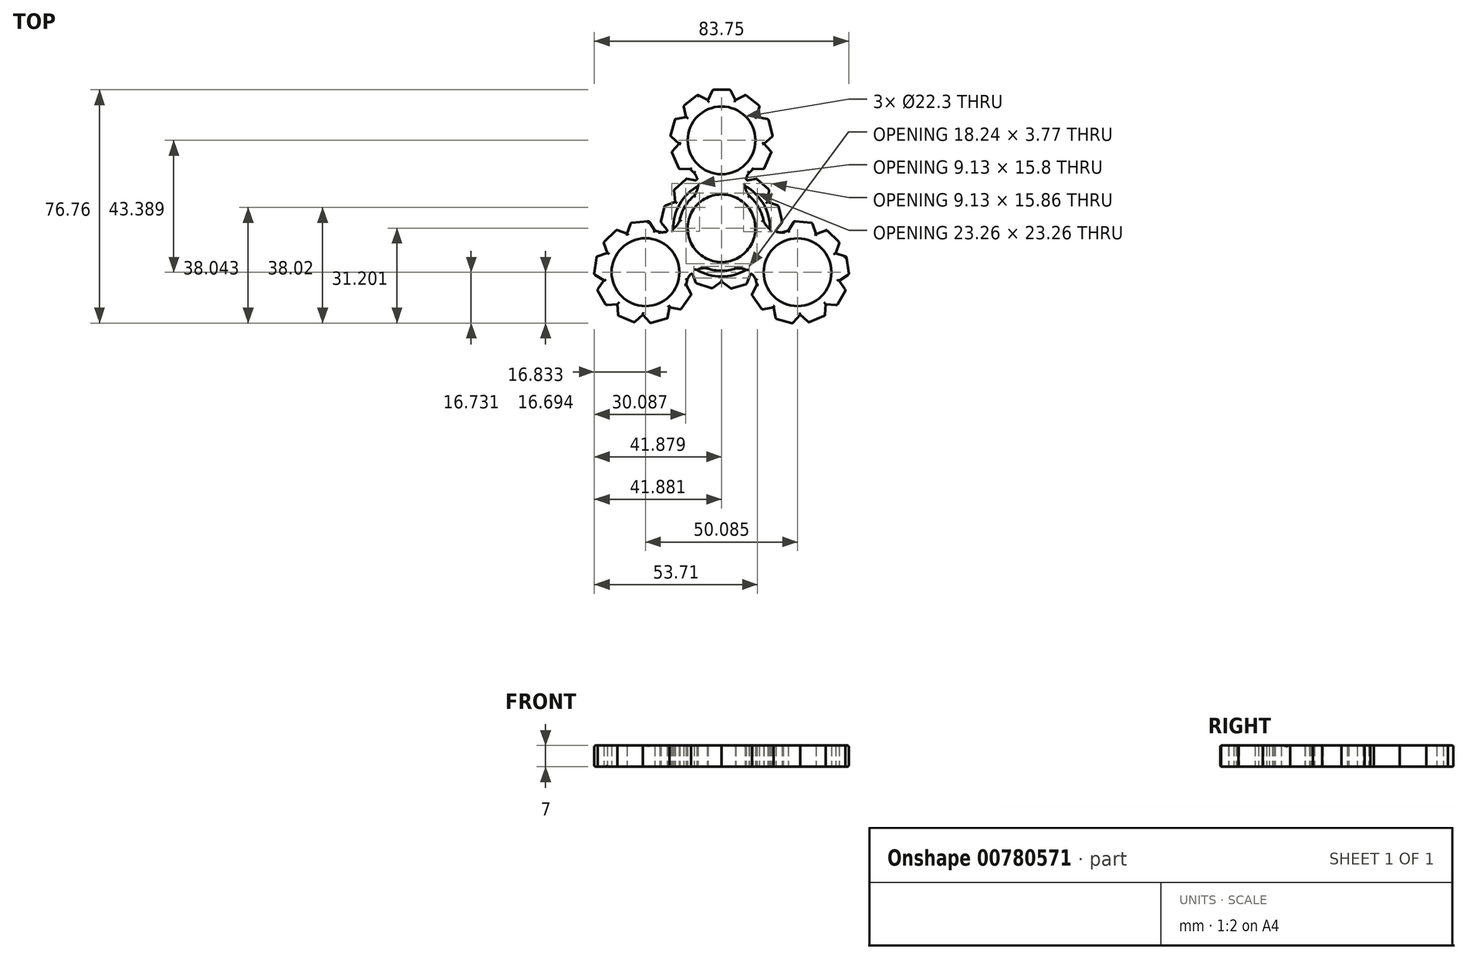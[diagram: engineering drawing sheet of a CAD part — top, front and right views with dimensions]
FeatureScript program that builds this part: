
annotation { "Feature Type Name" : "Feature", "Feature Type Description" : "" }
export const myFeature = defineFeature(function(context is Context, id is Id, definition is map)
    precondition{}
    {
        {
            var Q0;
            Q0=qCreatedBy(makeId("Top.planeOp"),FACE);
            var sketch = newSketch(context, id + "F0", { "sketchPlane" : qUnion([Q0])});
            skCircle(sketch, "E0", {"center": v(0, 0) * mm, "radius": 11.15 * mm});
            skCircle(sketch, "E1", {"center": v(0, 0) * mm, "radius": 14 * mm});
            skCircle(sketch, "E2", {"center": v(0, 28.9) * mm, "radius": 11.15 * mm});
            skCircle(sketch, "E3", {"center": v(0, 28.9) * mm, "radius": 14 * mm});
            skArc(sketch, "E4", {"start": v(-9.12, 10.62) * mm, "mid": v(-7.74, 14.4) * mm, "end": v(-9.05, 18.22) * mm});
            skArc(sketch, "E5", {"start": v(9.05, 18.22) * mm, "mid": v(7.74, 14.4) * mm, "end": v(9.12, 10.62) * mm});
            skLineSegment(sketch, "E6", {"start": v(-4.5, 42.16) * mm, "end": v(-2.88, 45.54) * mm});
            skLineSegment(sketch, "E7", {"start": v(-2.88, 45.54) * mm, "end": v(2.88, 45.54) * mm});
            skLineSegment(sketch, "E8", {"start": v(2.88, 45.54) * mm, "end": v(4.5, 42.16) * mm});
            skLineSegment(sketch, "E9", {"start": v(-11.7, 36.6) * mm, "end": v(-12.47, 40.26) * mm});
            skLineSegment(sketch, "E10", {"start": v(-12.47, 40.26) * mm, "end": v(-7.84, 43.85) * mm});
            skLineSegment(sketch, "E11", {"start": v(-7.84, 43.85) * mm, "end": v(-4.5, 42.16) * mm});
            skLineSegment(sketch, "E12.1", {"start": v(-11.7, 36.6) * mm, "end": v(-11.7, 36.6) * mm});
            skLineSegment(sketch, "E13.0", {"start": v(-11.7, 36.55) * mm, "end": v(-4.57, 42.03) * mm, "construction": true});
            skLineSegment(sketch, "E14", {"start": v(-13.95, 27.81) * mm, "end": v(-16.8, 30.24) * mm});
            skLineSegment(sketch, "E15", {"start": v(-16.8, 30.24) * mm, "end": v(-15.35, 35.9) * mm});
            skLineSegment(sketch, "E16", {"start": v(-15.35, 35.9) * mm, "end": v(-11.67, 36.62) * mm});
            skLineSegment(sketch, "E17.0", {"start": v(-13.95, 27.81) * mm, "end": v(-11.7, 36.6) * mm, "construction": true});
            skLineSegment(sketch, "E18", {"start": v(-10.26, 19.38) * mm, "end": v(-14, 19.55) * mm});
            skLineSegment(sketch, "E19", {"start": v(-14, 19.55) * mm, "end": v(-16.44, 25) * mm});
            skLineSegment(sketch, "E20", {"start": v(-16.44, 25) * mm, "end": v(-13.95, 27.81) * mm});
            skLineSegment(sketch, "E21.MirrorCS", {"start": v(12.47, 40.26) * mm, "end": v(7.84, 43.85) * mm});
            skLineSegment(sketch, "E22.MirrorCS", {"start": v(7.84, 43.85) * mm, "end": v(4.5, 42.16) * mm});
            skLineSegment(sketch, "E23.MirrorCS", {"start": v(11.7, 36.6) * mm, "end": v(12.47, 40.26) * mm});
            skLineSegment(sketch, "E24.MirrorCS", {"start": v(15.35, 35.9) * mm, "end": v(11.67, 36.62) * mm});
            skLineSegment(sketch, "E25.MirrorCS", {"start": v(16.8, 30.24) * mm, "end": v(15.35, 35.9) * mm});
            skLineSegment(sketch, "E26.MirrorCS", {"start": v(13.95, 27.81) * mm, "end": v(16.8, 30.24) * mm});
            skLineSegment(sketch, "E27.MirrorCS", {"start": v(16.44, 25) * mm, "end": v(13.95, 27.81) * mm});
            skLineSegment(sketch, "E28.MirrorCS", {"start": v(14, 19.55) * mm, "end": v(16.44, 25) * mm});
            skLineSegment(sketch, "E29.MirrorCS", {"start": v(10.26, 19.38) * mm, "end": v(14, 19.55) * mm});
            skLineSegment(sketch, "E30.1.0", {"start": v(-28.67, -30.94) * mm, "end": v(-34.1, -28.73) * mm});
            skLineSegment(sketch, "E30.1.1", {"start": v(-23.46, -31.26) * mm, "end": v(-25.92, -28.42) * mm});
            skLineSegment(sketch, "E30.1.2", {"start": v(-17.82, -29.69) * mm, "end": v(-23.46, -31.26) * mm});
            skLineSegment(sketch, "E30.1.3", {"start": v(-34.63, -0.57) * mm, "end": v(-38.81, -4.67) * mm});
            skLineSegment(sketch, "E30.1.4", {"start": v(-23.97, 2.34) * mm, "end": v(-29.9, 1.72) * mm});
            skLineSegment(sketch, "E30.1.5", {"start": v(-21.95, -0.81) * mm, "end": v(-23.97, 2.34) * mm});
            skCircle(sketch, "E30.1.6", {"center": v(-0.04, -0.01) * mm, "radius": 14 * mm});
            skLineSegment(sketch, "E30.1.7", {"start": v(-38.04, -25.27) * mm, "end": v(-40.92, -20.29) * mm});
            skLineSegment(sketch, "E30.1.8", {"start": v(-34.1, -28.73) * mm, "end": v(-34.3, -24.99) * mm});
            skLineSegment(sketch, "E30.1.9", {"start": v(-25.84, -28.43) * mm, "end": v(-34.16, -24.98) * mm, "construction": true});
            skLineSegment(sketch, "E30.1.10", {"start": v(-38.81, -4.67) * mm, "end": v(-37.58, -8.22) * mm});
            skArc(sketch, "E30.1.11", {"start": v(-20.34, -1.29) * mm, "mid": v(-16.39, -0.51) * mm, "end": v(-13.8, 2.58) * mm});
            skArc(sketch, "E30.1.12", {"start": v(-4.68, -13.22) * mm, "mid": v(-8.65, -13.92) * mm, "end": v(-11.3, -16.96) * mm});
            skCircle(sketch, "E30.1.13", {"center": v(-25.07, -14.46) * mm, "radius": 14 * mm});
            skCircle(sketch, "E30.1.14", {"center": v(-25.07, -14.46) * mm, "radius": 11.15 * mm});
            skLineSegment(sketch, "E30.1.15", {"start": v(-41.94, -15.14) * mm, "end": v(-38.8, -17.2) * mm});
            skCircle(sketch, "E30.1.16", {"center": v(-0.04, -0.01) * mm, "radius": 11.15 * mm});
            skLineSegment(sketch, "E30.1.17", {"start": v(-41.14, -9.34) * mm, "end": v(-41.94, -15.14) * mm});
            skLineSegment(sketch, "E30.1.18", {"start": v(-17.15, -26) * mm, "end": v(-25.88, -28.44) * mm, "construction": true});
            skLineSegment(sketch, "E30.1.19", {"start": v(-29.9, 1.72) * mm, "end": v(-31.1, -1.83) * mm});
            skLineSegment(sketch, "E30.1.20", {"start": v(-31.1, -1.83) * mm, "end": v(-34.63, -0.57) * mm});
            skLineSegment(sketch, "E30.1.21", {"start": v(-37.58, -8.18) * mm, "end": v(-41.14, -9.34) * mm});
            skLineSegment(sketch, "E30.1.22", {"start": v(-9.97, -21.92) * mm, "end": v(-13.47, -26.74) * mm});
            skLineSegment(sketch, "E30.1.23", {"start": v(-40.92, -20.29) * mm, "end": v(-38.8, -17.2) * mm});
            skLineSegment(sketch, "E30.1.24", {"start": v(-25.88, -28.44) * mm, "end": v(-28.67, -30.94) * mm});
            skLineSegment(sketch, "E30.1.25", {"start": v(-34.3, -24.99) * mm, "end": v(-38.04, -25.27) * mm});
            skLineSegment(sketch, "E30.1.26", {"start": v(-11.69, -18.58) * mm, "end": v(-9.97, -21.92) * mm});
            skLineSegment(sketch, "E30.1.27", {"start": v(-17.15, -26) * mm, "end": v(-17.82, -29.69) * mm});
            skLineSegment(sketch, "E30.1.28", {"start": v(-13.47, -26.74) * mm, "end": v(-17.15, -26) * mm});
            skLineSegment(sketch, "E30.2.0", {"start": v(41.1, -9.37) * mm, "end": v(41.89, -15.17) * mm});
            skLineSegment(sketch, "E30.2.1", {"start": v(38.76, -4.7) * mm, "end": v(37.53, -8.24) * mm});
            skLineSegment(sketch, "E30.2.2", {"start": v(34.58, -0.6) * mm, "end": v(38.76, -4.7) * mm});
            skLineSegment(sketch, "E30.2.3", {"start": v(17.78, -29.72) * mm, "end": v(23.41, -31.29) * mm});
            skLineSegment(sketch, "E30.2.4", {"start": v(9.92, -21.94) * mm, "end": v(13.42, -26.77) * mm});
            skLineSegment(sketch, "E30.2.5", {"start": v(11.64, -18.61) * mm, "end": v(9.92, -21.94) * mm});
            skCircle(sketch, "E30.2.6", {"center": v(-0.01, -0.04) * mm, "radius": 14 * mm});
            skLineSegment(sketch, "E30.2.7", {"start": v(40.87, -20.32) * mm, "end": v(37.99, -25.3) * mm});
            skLineSegment(sketch, "E30.2.8", {"start": v(41.89, -15.17) * mm, "end": v(38.75, -17.22) * mm});
            skLineSegment(sketch, "E30.2.9", {"start": v(37.5, -8.18) * mm, "end": v(38.67, -17.1) * mm, "construction": true});
            skLineSegment(sketch, "E30.2.10", {"start": v(23.41, -31.29) * mm, "end": v(25.87, -28.45) * mm});
            skArc(sketch, "E30.2.11", {"start": v(11.25, -16.98) * mm, "mid": v(8.6, -13.95) * mm, "end": v(4.63, -13.25) * mm});
            skArc(sketch, "E30.2.12", {"start": v(13.75, 2.55) * mm, "mid": v(16.34, -0.54) * mm, "end": v(20.3, -1.31) * mm});
            skCircle(sketch, "E30.2.13", {"center": v(25.02, -14.49) * mm, "radius": 14 * mm});
            skCircle(sketch, "E30.2.14", {"center": v(25.02, -14.49) * mm, "radius": 11.15 * mm});
            skLineSegment(sketch, "E30.2.15", {"start": v(34.04, -28.76) * mm, "end": v(34.25, -25.01) * mm});
            skCircle(sketch, "E30.2.16", {"center": v(-0.01, -0.04) * mm, "radius": 11.15 * mm});
            skLineSegment(sketch, "E30.2.17", {"start": v(28.63, -30.97) * mm, "end": v(34.04, -28.76) * mm});
            skLineSegment(sketch, "E30.2.18", {"start": v(31.05, -1.86) * mm, "end": v(37.53, -8.2) * mm, "construction": true});
            skLineSegment(sketch, "E30.2.19", {"start": v(13.42, -26.77) * mm, "end": v(17.1, -26.03) * mm});
            skLineSegment(sketch, "E30.2.20", {"start": v(17.1, -26.03) * mm, "end": v(17.78, -29.72) * mm});
            skLineSegment(sketch, "E30.2.21", {"start": v(25.83, -28.46) * mm, "end": v(28.63, -30.97) * mm});
            skLineSegment(sketch, "E30.2.22", {"start": v(23.93, 2.32) * mm, "end": v(29.86, 1.7) * mm});
            skLineSegment(sketch, "E30.2.23", {"start": v(37.99, -25.3) * mm, "end": v(34.25, -25.01) * mm});
            skLineSegment(sketch, "E30.2.24", {"start": v(37.53, -8.2) * mm, "end": v(41.1, -9.37) * mm});
            skLineSegment(sketch, "E30.2.25", {"start": v(38.75, -17.22) * mm, "end": v(40.87, -20.32) * mm});
            skLineSegment(sketch, "E30.2.26", {"start": v(21.9, -0.84) * mm, "end": v(23.93, 2.32) * mm});
            skLineSegment(sketch, "E30.2.27", {"start": v(31.05, -1.86) * mm, "end": v(34.58, -0.6) * mm});
            skLineSegment(sketch, "E30.2.28", {"start": v(29.86, 1.7) * mm, "end": v(31.05, -1.86) * mm});
            skPoint(sketch, "E30.center", {"position": v(-0.02, -0.02) * mm});
            skCircle(sketch, "E31", {"center": v(0, 0) * mm, "radius": 15.91 * mm});
            skCircle(sketch, "E32", {"center": v(0, 0) * mm, "radius": 17.5 * mm});
            skLineSegment(sketch, "E33.MirrorCS", {"start": v(11.54, 16.34) * mm, "end": v(7.86, 15.64) * mm});
            skLineSegment(sketch, "E34.MirrorCS", {"start": v(15.63, 12.67) * mm, "end": v(11.54, 16.34) * mm});
            skLineSegment(sketch, "E35.MirrorCS", {"start": v(15.22, 8.64) * mm, "end": v(15.63, 12.67) * mm});
            skLineSegment(sketch, "E36.MirrorCS", {"start": v(18.74, 7.35) * mm, "end": v(15.22, 8.64) * mm});
            skLineSegment(sketch, "E37.MirrorCS", {"start": v(20, 2) * mm, "end": v(18.74, 7.35) * mm});
            skLineSegment(sketch, "E38.MirrorCS", {"start": v(17.47, -1.05) * mm, "end": v(20, 2) * mm});
            skLineSegment(sketch, "E39.MirrorCS", {"start": v(-15.63, 12.67) * mm, "end": v(-11.54, 16.34) * mm});
            skLineSegment(sketch, "E40.MirrorCS", {"start": v(-11.54, 16.34) * mm, "end": v(-7.86, 15.64) * mm});
            skLineSegment(sketch, "E41.MirrorCS", {"start": v(-15.22, 8.64) * mm, "end": v(-15.63, 12.67) * mm});
            skLineSegment(sketch, "E42.MirrorCS", {"start": v(-18.74, 7.35) * mm, "end": v(-15.22, 8.64) * mm});
            skLineSegment(sketch, "E43.MirrorCS", {"start": v(-20, 2) * mm, "end": v(-18.74, 7.35) * mm});
            skLineSegment(sketch, "E44.MirrorCS", {"start": v(-17.47, -1.05) * mm, "end": v(-20, 2) * mm});
            skLineSegment(sketch, "E45.MirrorCS", {"start": v(-3.17, -19.8) * mm, "end": v(-8.4, -18.1) * mm});
            skLineSegment(sketch, "E46.MirrorCS", {"start": v(-8.4, -18.1) * mm, "end": v(-9.63, -14.61) * mm});
            skLineSegment(sketch, "E47.MirrorCS", {"start": v(0, -17.5) * mm, "end": v(-3.17, -19.8) * mm});
            skLineSegment(sketch, "E48.MirrorCS", {"start": v(3.04, -19.88) * mm, "end": v(0, -17.5) * mm});
            skLineSegment(sketch, "E49.MirrorCS", {"start": v(8.31, -18.3) * mm, "end": v(3.04, -19.88) * mm});
            skLineSegment(sketch, "E50.MirrorCS", {"start": v(9.58, -14.64) * mm, "end": v(8.31, -18.3) * mm});
            skSolve(sketch);
        }
        {
            var Q0;
            Q0=makeQuery(id+"F0.imprint","IMPRINT",FACE,{"disambiguationData":[TD([[makeQuery(id+"F0.imprint","IMPRINT",EDGE,{"derivedFrom":sQuery(id+"F0.wireOp",EDGE,"E30.2.7")}),-1.0]])]});
            var Q1;
            {var subQ4=sQuery(id+"F0.wireOp",EDGE,"E30.2.22");Q1=makeQuery(id+"F0.imprint","IMPRINT",FACE,{"disambiguationData":[TD([[makeQuery(id+"F0.imprint","IMPRINT",EDGE,{"derivedFrom":subQ4}),-1.0]])]});}
            var Q2;
            {var subQ0=sQuery(id+"F0.wireOp",EDGE,"E33.MirrorCS");Q2=makeQuery(id+"F0.imprint","IMPRINT",FACE,{"disambiguationData":[TD([[makeQuery(id+"F0.imprint","IMPRINT",EDGE,{"derivedFrom":subQ0}),1.0]])]});}
            var Q3;
            {var subQ1=sQuery(id+"F0.wireOp",EDGE,"E21.MirrorCS");Q3=makeQuery(id+"F0.imprint","IMPRINT",FACE,{"disambiguationData":[TD([[makeQuery(id+"F0.imprint","IMPRINT",EDGE,{"derivedFrom":subQ1}),1.0]])]});}
            var Q4;
            {var subQ1=sQuery(id+"F0.wireOp",EDGE,"E30.2.3");Q4=makeQuery(id+"F0.imprint","IMPRINT",FACE,{"disambiguationData":[TD([[makeQuery(id+"F0.imprint","IMPRINT",EDGE,{"derivedFrom":subQ1}),1.0]])]});}
            var Q5;
            {var subQ3=sQuery(id+"F0.wireOp",EDGE,"E31");var subQ5=sQuery(id+"F0.wireOp",EDGE,"E30.2.13");var subQ6=makeQuery(id+"F0.imprint","INTERSECT",VERTEX,{"disambiguationData":[OD(1.0)],"derivedFrom":[subQ5,subQ3]});Q5=makeQuery(id+"F0.imprint","IMPRINT",FACE,{"disambiguationData":[TD([[makeQuery(id+"F0.imprint","IMPRINT",EDGE,{"disambiguationData":[TD([[subQ6,-1.0]])],"derivedFrom":subQ5}),-1.0]])]});}
            var Q6;
            {var subQ0=sQuery(id+"F0.wireOp",EDGE,"E32");var subQ2=sQuery(id+"F0.wireOp",EDGE,"E30.1.11");var subQ3=makeQuery(id+"F0.imprint","INTERSECT",VERTEX,{"derivedFrom":[subQ2,subQ0]});Q6=makeQuery(id+"F0.imprint","IMPRINT",FACE,{"disambiguationData":[TD([[makeQuery(id+"F0.imprint","IMPRINT",EDGE,{"disambiguationData":[TD([[subQ3,-1.0]])],"derivedFrom":subQ2}),-1.0]])]});}
            var Q7;
            Q7=makeQuery(id+"F0.imprint","IMPRINT",FACE,{"disambiguationData":[TD([[makeQuery(id+"F0.imprint","IMPRINT",EDGE,{"derivedFrom":sQuery(id+"F0.wireOp",EDGE,"E45.MirrorCS")}),-1.0]])]});
            var Q8;
            {var subQ0=sQuery(id+"F0.wireOp",EDGE,"E30.2.12");var subQ1=sQuery(id+"F0.wireOp",EDGE,"E1");var subQ2=makeQuery(id+"F0.imprint","INTERSECT",VERTEX,{"derivedFrom":[subQ1,subQ0]});Q8=makeQuery(id+"F0.imprint","IMPRINT",FACE,{"disambiguationData":[TD([[makeQuery(id+"F0.imprint","IMPRINT",EDGE,{"disambiguationData":[TD([[subQ2,1.0]])],"derivedFrom":subQ1}),-1.0]])]});}
            var Q9;
            {var subQ0=sQuery(id+"F0.wireOp",EDGE,"E31");var subQ1=sQuery(id+"F0.wireOp",EDGE,"E30.1.12");var subQ2=makeQuery(id+"F0.imprint","INTERSECT",VERTEX,{"derivedFrom":[subQ1,subQ0]});Q9=makeQuery(id+"F0.imprint","IMPRINT",FACE,{"disambiguationData":[TD([[makeQuery(id+"F0.imprint","IMPRINT",EDGE,{"disambiguationData":[TD([[subQ2,-1.0]])],"derivedFrom":subQ0}),-1.0]])]});}
            var Q10;
            {var subQ5=sQuery(id+"F0.wireOp",EDGE,"E30.2.2");Q10=makeQuery(id+"F0.imprint","IMPRINT",FACE,{"disambiguationData":[TD([[makeQuery(id+"F0.imprint","IMPRINT",EDGE,{"derivedFrom":subQ5}),-1.0]])]});}
            var Q11;
            {var subQ0=sQuery(id+"F0.wireOp",EDGE,"E5");var subQ1=sQuery(id+"F0.wireOp",EDGE,"E1");var subQ2=makeQuery(id+"F0.imprint","INTERSECT",VERTEX,{"derivedFrom":[subQ1,subQ0]});Q11=makeQuery(id+"F0.imprint","IMPRINT",FACE,{"disambiguationData":[TD([[makeQuery(id+"F0.imprint","IMPRINT",EDGE,{"disambiguationData":[TD([[subQ2,-1.0]])],"derivedFrom":subQ1}),-1.0]])]});}
            var Q12;
            {var subQ0=sQuery(id+"F0.wireOp",EDGE,"E36.MirrorCS");Q12=makeQuery(id+"F0.imprint","IMPRINT",FACE,{"disambiguationData":[TD([[makeQuery(id+"F0.imprint","IMPRINT",EDGE,{"derivedFrom":subQ0}),1.0]])]});}
            var Q13;
            {var subQ0=sQuery(id+"F0.wireOp",EDGE,"E30.2.4");Q13=makeQuery(id+"F0.imprint","IMPRINT",FACE,{"disambiguationData":[TD([[makeQuery(id+"F0.imprint","IMPRINT",EDGE,{"derivedFrom":subQ0}),1.0]])]});}
            var Q14;
            {var subQ1=sQuery(id+"F0.wireOp",EDGE,"E42.MirrorCS");Q14=makeQuery(id+"F0.imprint","IMPRINT",FACE,{"disambiguationData":[TD([[makeQuery(id+"F0.imprint","IMPRINT",EDGE,{"derivedFrom":subQ1}),-1.0]])]});}
            var Q15;
            {var subQ1=sQuery(id+"F0.wireOp",EDGE,"E5");var subQ6=sQuery(id+"F0.wireOp",EDGE,"E31");var subQ8=makeQuery(id+"F0.imprint","INTERSECT",VERTEX,{"derivedFrom":[subQ1,subQ6]});Q15=makeQuery(id+"F0.imprint","IMPRINT",FACE,{"disambiguationData":[TD([[makeQuery(id+"F0.imprint","IMPRINT",EDGE,{"disambiguationData":[TD([[subQ8,1.0]])],"derivedFrom":subQ6}),-1.0]])]});}
            var Q16;
            {var subQ0=sQuery(id+"F0.wireOp",EDGE,"E31");var subQ1=sQuery(id+"F0.wireOp",EDGE,"E30.2.13");var subQ2=makeQuery(id+"F0.imprint","INTERSECT",VERTEX,{"disambiguationData":[OD(0.0)],"derivedFrom":[subQ1,subQ0]});Q16=makeQuery(id+"F0.imprint","IMPRINT",FACE,{"disambiguationData":[TD([[makeQuery(id+"F0.imprint","IMPRINT",EDGE,{"disambiguationData":[TD([[subQ2,-1.0]])],"derivedFrom":subQ1}),1.0]])]});}
            var Q17;
            {var subQ6=sQuery(id+"F0.wireOp",EDGE,"E30.1.0");Q17=makeQuery(id+"F0.imprint","IMPRINT",FACE,{"disambiguationData":[TD([[makeQuery(id+"F0.imprint","IMPRINT",EDGE,{"derivedFrom":subQ6}),-1.0]])]});}
            var Q18;
            {var subQ0=sQuery(id+"F0.wireOp",EDGE,"E32");var subQ5=sQuery(id+"F0.wireOp",EDGE,"E30.1.13");var subQ7=makeQuery(id+"F0.imprint","INTERSECT",VERTEX,{"disambiguationData":[OD(0.0)],"derivedFrom":[subQ5,subQ0]});Q18=makeQuery(id+"F0.imprint","IMPRINT",FACE,{"disambiguationData":[TD([[makeQuery(id+"F0.imprint","IMPRINT",EDGE,{"disambiguationData":[TD([[subQ7,-1.0]])],"derivedFrom":subQ5}),-1.0]])]});}
            var Q19;
            Q19=makeQuery(id+"F0.imprint","IMPRINT",FACE,{"disambiguationData":[TD([[makeQuery(id+"F0.imprint","IMPRINT",EDGE,{"derivedFrom":sQuery(id+"F0.wireOp",EDGE,"E30.1.14")}),-1.0]])]});
            var Q20;
            {var subQ6=sQuery(id+"F0.wireOp",EDGE,"E30.2.0");Q20=makeQuery(id+"F0.imprint","IMPRINT",FACE,{"disambiguationData":[TD([[makeQuery(id+"F0.imprint","IMPRINT",EDGE,{"derivedFrom":subQ6}),-1.0]])]});}
            var Q21;
            {var subQ0=sQuery(id+"F0.wireOp",EDGE,"E31");var subQ1=sQuery(id+"F0.wireOp",EDGE,"E3");var subQ2=makeQuery(id+"F0.imprint","INTERSECT",VERTEX,{"disambiguationData":[OD(1.0)],"derivedFrom":[subQ1,subQ0]});Q21=makeQuery(id+"F0.imprint","IMPRINT",FACE,{"disambiguationData":[TD([[makeQuery(id+"F0.imprint","IMPRINT",EDGE,{"disambiguationData":[TD([[subQ2,-1.0]])],"derivedFrom":subQ1}),-1.0]])]});}
            var Q22;
            {var subQ6=sQuery(id+"F0.wireOp",EDGE,"E30.1.15");Q22=makeQuery(id+"F0.imprint","IMPRINT",FACE,{"disambiguationData":[TD([[makeQuery(id+"F0.imprint","IMPRINT",EDGE,{"derivedFrom":subQ6}),1.0]])]});}
            var Q23;
            {var subQ0=sQuery(id+"F0.wireOp",EDGE,"E30.1.16");var subQ1=sQuery(id+"F0.wireOp",EDGE,"E0");var subQ2=makeQuery(id+"F0.imprint","INTERSECT",VERTEX,{"disambiguationData":[OD(0.0)],"derivedFrom":[subQ1,subQ0]});Q23=makeQuery(id+"F0.imprint","IMPRINT",FACE,{"disambiguationData":[TD([[makeQuery(id+"F0.imprint","IMPRINT",EDGE,{"disambiguationData":[TD([[subQ2,1.0]])],"derivedFrom":subQ1}),-1.0]])]});}
            var Q24;
            {var subQ0=sQuery(id+"F0.wireOp",EDGE,"E48.MirrorCS");Q24=makeQuery(id+"F0.imprint","IMPRINT",FACE,{"disambiguationData":[TD([[makeQuery(id+"F0.imprint","IMPRINT",EDGE,{"derivedFrom":subQ0}),-1.0]])]});}
            var Q25;
            {var subQ4=sQuery(id+"F0.wireOp",EDGE,"E30.1.22");Q25=makeQuery(id+"F0.imprint","IMPRINT",FACE,{"disambiguationData":[TD([[makeQuery(id+"F0.imprint","IMPRINT",EDGE,{"derivedFrom":subQ4}),-1.0]])]});}
            var Q26;
            {var subQ0=sQuery(id+"F0.wireOp",EDGE,"E31");var subQ1=sQuery(id+"F0.wireOp",EDGE,"E4");var subQ2=makeQuery(id+"F0.imprint","INTERSECT",VERTEX,{"derivedFrom":[subQ1,subQ0]});Q26=makeQuery(id+"F0.imprint","IMPRINT",FACE,{"disambiguationData":[TD([[makeQuery(id+"F0.imprint","IMPRINT",EDGE,{"disambiguationData":[TD([[subQ2,-1.0]])],"derivedFrom":subQ1}),1.0]])]});}
            var Q27;
            Q27=makeQuery(id+"F0.imprint","IMPRINT",FACE,{"disambiguationData":[TD([[makeQuery(id+"F0.imprint","IMPRINT",EDGE,{"derivedFrom":sQuery(id+"F0.wireOp",EDGE,"E30.1.7")}),-1.0]])]});
            var Q28;
            {var subQ4=sQuery(id+"F0.wireOp",EDGE,"E28.MirrorCS");Q28=makeQuery(id+"F0.imprint","IMPRINT",FACE,{"disambiguationData":[TD([[makeQuery(id+"F0.imprint","IMPRINT",EDGE,{"derivedFrom":subQ4}),1.0]])]});}
            var Q29;
            Q29=makeQuery(id+"F0.imprint","IMPRINT",FACE,{"disambiguationData":[TD([[makeQuery(id+"F0.imprint","IMPRINT",EDGE,{"derivedFrom":sQuery(id+"F0.wireOp",EDGE,"E2")}),-1.0]])]});
            var Q30;
            {var subQ0=sQuery(id+"F0.wireOp",EDGE,"E32");var subQ2=sQuery(id+"F0.wireOp",EDGE,"E3");var subQ3=makeQuery(id+"F0.imprint","INTERSECT",VERTEX,{"disambiguationData":[OD(0.0)],"derivedFrom":[subQ2,subQ0]});Q30=makeQuery(id+"F0.imprint","IMPRINT",FACE,{"disambiguationData":[TD([[makeQuery(id+"F0.imprint","IMPRINT",EDGE,{"disambiguationData":[TD([[subQ3,-1.0]])],"derivedFrom":subQ2}),-1.0]])]});}
            var Q31;
            {var subQ0=sQuery(id+"F0.wireOp",EDGE,"E32");var subQ1=sQuery(id+"F0.wireOp",EDGE,"E3");var subQ2=makeQuery(id+"F0.imprint","INTERSECT",VERTEX,{"disambiguationData":[OD(0.0)],"derivedFrom":[subQ1,subQ0]});Q31=makeQuery(id+"F0.imprint","IMPRINT",FACE,{"disambiguationData":[TD([[makeQuery(id+"F0.imprint","IMPRINT",EDGE,{"disambiguationData":[TD([[subQ2,-1.0]])],"derivedFrom":subQ1}),1.0]])]});}
            var Q32;
            {var subQ0=sQuery(id+"F0.wireOp",EDGE,"E31");var subQ1=sQuery(id+"F0.wireOp",EDGE,"E30.1.13");var subQ2=makeQuery(id+"F0.imprint","INTERSECT",VERTEX,{"disambiguationData":[OD(0.0)],"derivedFrom":[subQ1,subQ0]});Q32=makeQuery(id+"F0.imprint","IMPRINT",FACE,{"disambiguationData":[TD([[makeQuery(id+"F0.imprint","IMPRINT",EDGE,{"disambiguationData":[TD([[subQ2,-1.0]])],"derivedFrom":subQ1}),1.0]])]});}
            var Q33;
            {var subQ1=sQuery(id+"F0.wireOp",EDGE,"E39.MirrorCS");Q33=makeQuery(id+"F0.imprint","IMPRINT",FACE,{"disambiguationData":[TD([[makeQuery(id+"F0.imprint","IMPRINT",EDGE,{"derivedFrom":subQ1}),-1.0]])]});}
            var Q34;
            {var subQ0=sQuery(id+"F0.wireOp",EDGE,"E32");var subQ5=sQuery(id+"F0.wireOp",EDGE,"E30.2.13");var subQ6=makeQuery(id+"F0.imprint","INTERSECT",VERTEX,{"disambiguationData":[OD(0.0)],"derivedFrom":[subQ5,subQ0]});Q34=makeQuery(id+"F0.imprint","IMPRINT",FACE,{"disambiguationData":[TD([[makeQuery(id+"F0.imprint","IMPRINT",EDGE,{"disambiguationData":[TD([[subQ6,-1.0]])],"derivedFrom":subQ5}),-1.0]])]});}
            var Q35;
            {var subQ0=sQuery(id+"F0.wireOp",EDGE,"E32");var subQ1=sQuery(id+"F0.wireOp",EDGE,"E30.1.13");var subQ2=makeQuery(id+"F0.imprint","INTERSECT",VERTEX,{"disambiguationData":[OD(0.0)],"derivedFrom":[subQ1,subQ0]});Q35=makeQuery(id+"F0.imprint","IMPRINT",FACE,{"disambiguationData":[TD([[makeQuery(id+"F0.imprint","IMPRINT",EDGE,{"disambiguationData":[TD([[subQ2,-1.0]])],"derivedFrom":subQ1}),1.0]])]});}
            var Q36;
            {var subQ1=sQuery(id+"F0.wireOp",EDGE,"E30.2.15");Q36=makeQuery(id+"F0.imprint","IMPRINT",FACE,{"disambiguationData":[TD([[makeQuery(id+"F0.imprint","IMPRINT",EDGE,{"derivedFrom":subQ1}),1.0]])]});}
            var Q37;
            {var subQ0=sQuery(id+"F0.wireOp",EDGE,"E15");Q37=makeQuery(id+"F0.imprint","IMPRINT",FACE,{"disambiguationData":[TD([[makeQuery(id+"F0.imprint","IMPRINT",EDGE,{"derivedFrom":subQ0}),-1.0]])]});}
            var Q38;
            Q38=makeQuery(id+"F0.imprint","IMPRINT",FACE,{"disambiguationData":[TD([[makeQuery(id+"F0.imprint","IMPRINT",EDGE,{"derivedFrom":sQuery(id+"F0.wireOp",EDGE,"E30.2.14")}),-1.0]])]});
            var Q39;
            {var subQ5=sQuery(id+"F0.wireOp",EDGE,"E30.1.2");Q39=makeQuery(id+"F0.imprint","IMPRINT",FACE,{"disambiguationData":[TD([[makeQuery(id+"F0.imprint","IMPRINT",EDGE,{"derivedFrom":subQ5}),-1.0]])]});}
            var Q40;
            {var subQ0=sQuery(id+"F0.wireOp",EDGE,"E25.MirrorCS");Q40=makeQuery(id+"F0.imprint","IMPRINT",FACE,{"disambiguationData":[TD([[makeQuery(id+"F0.imprint","IMPRINT",EDGE,{"derivedFrom":subQ0}),1.0]])]});}
            var Q41;
            {var subQ4=sQuery(id+"F0.wireOp",EDGE,"E30.1.11");var subQ5=sQuery(id+"F0.wireOp",EDGE,"E30.1.6");var subQ6=makeQuery(id+"F0.imprint","INTERSECT",VERTEX,{"derivedFrom":[subQ5,subQ4]});Q41=makeQuery(id+"F0.imprint","IMPRINT",FACE,{"disambiguationData":[TD([[makeQuery(id+"F0.imprint","IMPRINT",EDGE,{"disambiguationData":[TD([[subQ6,-1.0]])],"derivedFrom":subQ5}),-1.0]])]});}
            var Q42;
            {var subQ0=sQuery(id+"F0.wireOp",EDGE,"E6");Q42=makeQuery(id+"F0.imprint","IMPRINT",FACE,{"disambiguationData":[TD([[makeQuery(id+"F0.imprint","IMPRINT",EDGE,{"derivedFrom":subQ0}),-1.0]])]});}
            var Q43;
            {var subQ2=sQuery(id+"F0.wireOp",EDGE,"E4");var subQ4=sQuery(id+"F0.wireOp",EDGE,"E1");var subQ5=makeQuery(id+"F0.imprint","INTERSECT",VERTEX,{"derivedFrom":[subQ4,subQ2]});Q43=makeQuery(id+"F0.imprint","IMPRINT",FACE,{"disambiguationData":[TD([[makeQuery(id+"F0.imprint","IMPRINT",EDGE,{"disambiguationData":[TD([[subQ5,-1.0]])],"derivedFrom":subQ4}),-1.0]])]});}
            var Q44;
            {var subQ0=sQuery(id+"F0.wireOp",EDGE,"E32");var subQ1=sQuery(id+"F0.wireOp",EDGE,"E30.2.13");var subQ2=makeQuery(id+"F0.imprint","INTERSECT",VERTEX,{"disambiguationData":[OD(0.0)],"derivedFrom":[subQ1,subQ0]});Q44=makeQuery(id+"F0.imprint","IMPRINT",FACE,{"disambiguationData":[TD([[makeQuery(id+"F0.imprint","IMPRINT",EDGE,{"disambiguationData":[TD([[subQ2,-1.0]])],"derivedFrom":subQ1}),1.0]])]});}
            var Q45;
            {var subQ1=sQuery(id+"F0.wireOp",EDGE,"E10");Q45=makeQuery(id+"F0.imprint","IMPRINT",FACE,{"disambiguationData":[TD([[makeQuery(id+"F0.imprint","IMPRINT",EDGE,{"derivedFrom":subQ1}),-1.0]])]});}
            var Q46;
            {var subQ5=sQuery(id+"F0.wireOp",EDGE,"E30.1.3");Q46=makeQuery(id+"F0.imprint","IMPRINT",FACE,{"disambiguationData":[TD([[makeQuery(id+"F0.imprint","IMPRINT",EDGE,{"derivedFrom":subQ5}),1.0]])]});}
            var Q47;
            {var subQ0=sQuery(id+"F0.wireOp",EDGE,"E18");Q47=makeQuery(id+"F0.imprint","IMPRINT",FACE,{"disambiguationData":[TD([[makeQuery(id+"F0.imprint","IMPRINT",EDGE,{"derivedFrom":subQ0}),-1.0]])]});}
            var Q48;
            {var subQ0=sQuery(id+"F0.wireOp",EDGE,"E30.1.4");Q48=makeQuery(id+"F0.imprint","IMPRINT",FACE,{"disambiguationData":[TD([[makeQuery(id+"F0.imprint","IMPRINT",EDGE,{"derivedFrom":subQ0}),1.0]])]});}
            var Q49;
            {var subQ0=sQuery(id+"F0.wireOp",EDGE,"E30.1.13");var subQ1=sQuery(id+"F0.wireOp",EDGE,"E30.1.11");var subQ2=makeQuery(id+"F0.imprint","INTERSECT",VERTEX,{"derivedFrom":[subQ1,subQ0]});Q49=makeQuery(id+"F0.imprint","IMPRINT",FACE,{"disambiguationData":[TD([[makeQuery(id+"F0.imprint","IMPRINT",EDGE,{"disambiguationData":[TD([[subQ2,-1.0]])],"derivedFrom":subQ1}),-1.0]])]});}
            var Q50;
            {var subQ0=sQuery(id+"F0.wireOp",EDGE,"E4");var subQ1=sQuery(id+"F0.wireOp",EDGE,"E3");var subQ2=makeQuery(id+"F0.imprint","INTERSECT",VERTEX,{"derivedFrom":[subQ1,subQ0]});Q50=makeQuery(id+"F0.imprint","IMPRINT",FACE,{"disambiguationData":[TD([[makeQuery(id+"F0.imprint","IMPRINT",EDGE,{"disambiguationData":[TD([[subQ2,-1.0]])],"derivedFrom":subQ1}),-1.0]])]});}
            var Q51;
            {var subQ0=sQuery(id+"F0.wireOp",EDGE,"E30.1.13");var subQ1=sQuery(id+"F0.wireOp",EDGE,"E30.1.12");var subQ2=makeQuery(id+"F0.imprint","INTERSECT",VERTEX,{"derivedFrom":[subQ1,subQ0]});Q51=makeQuery(id+"F0.imprint","IMPRINT",FACE,{"disambiguationData":[TD([[makeQuery(id+"F0.imprint","IMPRINT",EDGE,{"disambiguationData":[TD([[subQ2,-1.0]])],"derivedFrom":subQ0}),-1.0]])]});}
            var Q52;
            {var subQ0=sQuery(id+"F0.wireOp",EDGE,"E30.1.6");var subQ1=sQuery(id+"F0.wireOp",EDGE,"E1");var subQ2=makeQuery(id+"F0.imprint","INTERSECT",VERTEX,{"disambiguationData":[OD(1.0)],"derivedFrom":[subQ1,subQ0]});Q52=makeQuery(id+"F0.imprint","IMPRINT",FACE,{"disambiguationData":[TD([[makeQuery(id+"F0.imprint","IMPRINT",EDGE,{"disambiguationData":[TD([[subQ2,-1.0]])],"derivedFrom":subQ1}),1.0]])]});}
            var Q53;
            {var subQ0=sQuery(id+"F0.wireOp",EDGE,"E30.1.16");var subQ1=sQuery(id+"F0.wireOp",EDGE,"E0");var subQ2=makeQuery(id+"F0.imprint","INTERSECT",VERTEX,{"disambiguationData":[OD(0.0)],"derivedFrom":[subQ1,subQ0]});Q53=makeQuery(id+"F0.imprint","IMPRINT",FACE,{"disambiguationData":[TD([[makeQuery(id+"F0.imprint","IMPRINT",EDGE,{"disambiguationData":[TD([[subQ2,1.0]])],"derivedFrom":subQ1}),1.0]])]});}
            var Q54;
            {var subQ0=sQuery(id+"F0.wireOp",EDGE,"E30.2.6");var subQ1=sQuery(id+"F0.wireOp",EDGE,"E1");var subQ2=makeQuery(id+"F0.imprint","INTERSECT",VERTEX,{"disambiguationData":[OD(0.0)],"derivedFrom":[subQ1,subQ0]});Q54=makeQuery(id+"F0.imprint","IMPRINT",FACE,{"disambiguationData":[TD([[makeQuery(id+"F0.imprint","IMPRINT",EDGE,{"disambiguationData":[TD([[subQ2,-1.0]])],"derivedFrom":subQ1}),-1.0]])]});}
            var Q55;
            {var subQ0=sQuery(id+"F0.wireOp",EDGE,"E30.1.16");var subQ1=sQuery(id+"F0.wireOp",EDGE,"E0");var subQ2=makeQuery(id+"F0.imprint","INTERSECT",VERTEX,{"disambiguationData":[OD(1.0)],"derivedFrom":[subQ1,subQ0]});Q55=makeQuery(id+"F0.imprint","IMPRINT",FACE,{"disambiguationData":[TD([[makeQuery(id+"F0.imprint","IMPRINT",EDGE,{"disambiguationData":[TD([[subQ2,-1.0]])],"derivedFrom":subQ1}),-1.0]])]});}
            var Q56;
            {var subQ0=sQuery(id+"F0.wireOp",EDGE,"E5");var subQ1=sQuery(id+"F0.wireOp",EDGE,"E3");var subQ2=makeQuery(id+"F0.imprint","INTERSECT",VERTEX,{"derivedFrom":[subQ1,subQ0]});Q56=makeQuery(id+"F0.imprint","IMPRINT",FACE,{"disambiguationData":[TD([[makeQuery(id+"F0.imprint","IMPRINT",EDGE,{"disambiguationData":[TD([[subQ2,1.0]])],"derivedFrom":subQ1}),-1.0]])]});}
            var Q57;
            {var subQ0=sQuery(id+"F0.wireOp",EDGE,"E30.1.16");var subQ1=sQuery(id+"F0.wireOp",EDGE,"E0");var subQ2=makeQuery(id+"F0.imprint","INTERSECT",VERTEX,{"disambiguationData":[OD(1.0)],"derivedFrom":[subQ1,subQ0]});Q57=makeQuery(id+"F0.imprint","IMPRINT",FACE,{"disambiguationData":[TD([[makeQuery(id+"F0.imprint","IMPRINT",EDGE,{"disambiguationData":[TD([[subQ2,-1.0]])],"derivedFrom":subQ1}),1.0]])]});}
            var Q58;
            {var subQ0=sQuery(id+"F0.wireOp",EDGE,"E1");var subQ1=makeQuery(id+"F0.imprint","INTERSECT",VERTEX,{"derivedFrom":[subQ0,sQuery(id+"F0.wireOp",EDGE,"E4")]});Q58=makeQuery(id+"F0.imprint","IMPRINT",FACE,{"disambiguationData":[TD([[makeQuery(id+"F0.imprint","IMPRINT",EDGE,{"disambiguationData":[TD([[subQ1,1.0]])],"derivedFrom":subQ0}),1.0]])]});}
            var Q59;
            {var subQ0=sQuery(id+"F0.wireOp",EDGE,"E30.1.12");var subQ1=sQuery(id+"F0.wireOp",EDGE,"E30.1.6");var subQ2=makeQuery(id+"F0.imprint","INTERSECT",VERTEX,{"derivedFrom":[subQ1,subQ0]});Q59=makeQuery(id+"F0.imprint","IMPRINT",FACE,{"disambiguationData":[TD([[makeQuery(id+"F0.imprint","IMPRINT",EDGE,{"disambiguationData":[TD([[subQ2,1.0]])],"derivedFrom":subQ1}),-1.0]])]});}
            var Q60;
            {var subQ0=sQuery(id+"F0.wireOp",EDGE,"E1");var subQ1=makeQuery(id+"F0.imprint","INTERSECT",VERTEX,{"derivedFrom":[subQ0,sQuery(id+"F0.wireOp",EDGE,"E5")]});Q60=makeQuery(id+"F0.imprint","IMPRINT",FACE,{"disambiguationData":[TD([[makeQuery(id+"F0.imprint","IMPRINT",EDGE,{"disambiguationData":[TD([[subQ1,1.0]])],"derivedFrom":subQ0}),1.0]])]});}
            var Q61;
            {var subQ0=sQuery(id+"F0.wireOp",EDGE,"E30.2.16");var subQ1=sQuery(id+"F0.wireOp",EDGE,"E0");var subQ2=makeQuery(id+"F0.imprint","INTERSECT",VERTEX,{"disambiguationData":[OD(0.0)],"derivedFrom":[subQ1,subQ0]});Q61=makeQuery(id+"F0.imprint","IMPRINT",FACE,{"disambiguationData":[TD([[makeQuery(id+"F0.imprint","IMPRINT",EDGE,{"disambiguationData":[TD([[subQ2,1.0]])],"derivedFrom":subQ1}),-1.0]])]});}
            var Q62;
            {var subQ0=sQuery(id+"F0.wireOp",EDGE,"E31");var subQ1=sQuery(id+"F0.wireOp",EDGE,"E3");var subQ2=makeQuery(id+"F0.imprint","INTERSECT",VERTEX,{"disambiguationData":[OD(0.0)],"derivedFrom":[subQ1,subQ0]});Q62=makeQuery(id+"F0.imprint","IMPRINT",FACE,{"disambiguationData":[TD([[makeQuery(id+"F0.imprint","IMPRINT",EDGE,{"disambiguationData":[TD([[subQ2,-1.0]])],"derivedFrom":subQ1}),1.0]])]});}
            var Q63;
            {var subQ0=sQuery(id+"F0.wireOp",EDGE,"E30.2.13");var subQ1=sQuery(id+"F0.wireOp",EDGE,"E30.2.12");var subQ2=makeQuery(id+"F0.imprint","INTERSECT",VERTEX,{"derivedFrom":[subQ1,subQ0]});Q63=makeQuery(id+"F0.imprint","IMPRINT",FACE,{"disambiguationData":[TD([[makeQuery(id+"F0.imprint","IMPRINT",EDGE,{"disambiguationData":[TD([[subQ2,-1.0]])],"derivedFrom":subQ0}),-1.0]])]});}
            var Q64;
            {var subQ4=sQuery(id+"F0.wireOp",EDGE,"E30.1.6");var subQ5=sQuery(id+"F0.wireOp",EDGE,"E1");var subQ6=makeQuery(id+"F0.imprint","INTERSECT",VERTEX,{"disambiguationData":[OD(1.0)],"derivedFrom":[subQ5,subQ4]});Q64=makeQuery(id+"F0.imprint","IMPRINT",FACE,{"disambiguationData":[TD([[makeQuery(id+"F0.imprint","IMPRINT",EDGE,{"disambiguationData":[TD([[subQ6,-1.0]])],"derivedFrom":subQ5}),-1.0]])]});}
            var Q65;
            {var subQ1=sQuery(id+"F0.wireOp",EDGE,"E30.2.11");var subQ3=sQuery(id+"F0.wireOp",EDGE,"E30.2.13");var subQ4=makeQuery(id+"F0.imprint","INTERSECT",VERTEX,{"derivedFrom":[subQ1,subQ3]});Q65=makeQuery(id+"F0.imprint","IMPRINT",FACE,{"disambiguationData":[TD([[makeQuery(id+"F0.imprint","IMPRINT",EDGE,{"disambiguationData":[TD([[subQ4,1.0]])],"derivedFrom":subQ3}),-1.0]])]});}
            var Q66;
            {var subQ0=sQuery(id+"F0.wireOp",EDGE,"E4");var subQ1=sQuery(id+"F0.wireOp",EDGE,"E1");var subQ2=makeQuery(id+"F0.imprint","INTERSECT",VERTEX,{"derivedFrom":[subQ1,subQ0]});Q66=makeQuery(id+"F0.imprint","IMPRINT",FACE,{"disambiguationData":[TD([[makeQuery(id+"F0.imprint","IMPRINT",EDGE,{"disambiguationData":[TD([[subQ2,1.0]])],"derivedFrom":subQ1}),-1.0]])]});}
            var Q67;
            {var subQ0=sQuery(id+"F0.wireOp",EDGE,"E30.1.19");var subQ1=sQuery(id+"F0.wireOp",EDGE,"E30.1.13");var subQ2=makeQuery(id+"F0.imprint","INTERSECT",VERTEX,{"derivedFrom":[subQ1,subQ0]});Q67=makeQuery(id+"F0.imprint","IMPRINT",FACE,{"disambiguationData":[TD([[makeQuery(id+"F0.imprint","IMPRINT",EDGE,{"disambiguationData":[TD([[subQ2,-1.0]])],"derivedFrom":subQ1}),1.0]])]});}
            var Q68;
            {var subQ0=sQuery(id+"F0.wireOp",EDGE,"E30.1.21");var subQ1=sQuery(id+"F0.wireOp",EDGE,"E30.1.10");var subQ2=makeQuery(id+"F0.imprint","INTERSECT",VERTEX,{"derivedFrom":[subQ1,subQ0]});Q68=makeQuery(id+"F0.imprint","IMPRINT",FACE,{"disambiguationData":[TD([[makeQuery(id+"F0.imprint","IMPRINT",EDGE,{"disambiguationData":[TD([[subQ2,-1.0]])],"derivedFrom":subQ1}),1.0]])]});}
            var Q69;
            {var subQ0=sQuery(id+"F0.wireOp",EDGE,"E24.MirrorCS");var subQ1=sQuery(id+"F0.wireOp",EDGE,"E3");var subQ2=makeQuery(id+"F0.imprint","INTERSECT",VERTEX,{"derivedFrom":[subQ1,subQ0]});Q69=makeQuery(id+"F0.imprint","IMPRINT",FACE,{"disambiguationData":[TD([[makeQuery(id+"F0.imprint","IMPRINT",EDGE,{"disambiguationData":[TD([[subQ2,1.0]])],"derivedFrom":subQ1}),-1.0]])]});}
            var Q70;
            {var subQ0=sQuery(id+"F0.wireOp",EDGE,"E30.2.19");var subQ1=sQuery(id+"F0.wireOp",EDGE,"E30.2.13");var subQ2=makeQuery(id+"F0.imprint","INTERSECT",VERTEX,{"derivedFrom":[subQ1,subQ0]});Q70=makeQuery(id+"F0.imprint","IMPRINT",FACE,{"disambiguationData":[TD([[makeQuery(id+"F0.imprint","IMPRINT",EDGE,{"disambiguationData":[TD([[subQ2,-1.0]])],"derivedFrom":subQ1}),1.0]])]});}
            var Q71;
            {var subQ0=sQuery(id+"F0.wireOp",EDGE,"E40.MirrorCS");var subQ1=sQuery(id+"F0.wireOp",EDGE,"E4");var subQ2=makeQuery(id+"F0.imprint","INTERSECT",VERTEX,{"derivedFrom":[subQ1,subQ0]});Q71=makeQuery(id+"F0.imprint","IMPRINT",FACE,{"disambiguationData":[TD([[makeQuery(id+"F0.imprint","IMPRINT",EDGE,{"disambiguationData":[TD([[subQ2,1.0]])],"derivedFrom":subQ1}),-1.0]])]});}
            var Q72;
            {var subQ0=sQuery(id+"F0.wireOp",EDGE,"E30.2.16");var subQ1=sQuery(id+"F0.wireOp",EDGE,"E0");var subQ2=makeQuery(id+"F0.imprint","INTERSECT",VERTEX,{"disambiguationData":[OD(0.0)],"derivedFrom":[subQ1,subQ0]});Q72=makeQuery(id+"F0.imprint","IMPRINT",FACE,{"disambiguationData":[TD([[makeQuery(id+"F0.imprint","IMPRINT",EDGE,{"disambiguationData":[TD([[subQ2,-1.0]])],"derivedFrom":subQ1}),-1.0]])]});}
            var Q73;
            {var subQ0=sQuery(id+"F0.wireOp",EDGE,"E30.2.12");var subQ1=sQuery(id+"F0.wireOp",EDGE,"E1");var subQ2=makeQuery(id+"F0.imprint","INTERSECT",VERTEX,{"derivedFrom":[subQ1,subQ0]});Q73=makeQuery(id+"F0.imprint","IMPRINT",FACE,{"disambiguationData":[TD([[makeQuery(id+"F0.imprint","IMPRINT",EDGE,{"disambiguationData":[TD([[subQ2,1.0]])],"derivedFrom":subQ1}),1.0]])]});}
            var Q74;
            {var subQ0=sQuery(id+"F0.wireOp",EDGE,"E30.2.16");var subQ1=sQuery(id+"F0.wireOp",EDGE,"E0");var subQ2=makeQuery(id+"F0.imprint","INTERSECT",VERTEX,{"disambiguationData":[OD(0.0)],"derivedFrom":[subQ1,subQ0]});Q74=makeQuery(id+"F0.imprint","IMPRINT",FACE,{"disambiguationData":[TD([[makeQuery(id+"F0.imprint","IMPRINT",EDGE,{"disambiguationData":[TD([[subQ2,1.0]])],"derivedFrom":subQ1}),1.0]])]});}
            var Q75;
            {var subQ0=sQuery(id+"F0.wireOp",EDGE,"E44.MirrorCS");var subQ1=sQuery(id+"F0.wireOp",EDGE,"E30.1.11");var subQ2=makeQuery(id+"F0.imprint","INTERSECT",VERTEX,{"derivedFrom":[subQ1,subQ0]});Q75=makeQuery(id+"F0.imprint","IMPRINT",FACE,{"disambiguationData":[TD([[makeQuery(id+"F0.imprint","IMPRINT",EDGE,{"disambiguationData":[TD([[subQ2,-1.0]])],"derivedFrom":subQ1}),-1.0]])]});}
            var Q76;
            {var subQ0=sQuery(id+"F0.wireOp",EDGE,"E30.2.21");var subQ1=sQuery(id+"F0.wireOp",EDGE,"E30.2.10");var subQ2=makeQuery(id+"F0.imprint","INTERSECT",VERTEX,{"derivedFrom":[subQ1,subQ0]});Q76=makeQuery(id+"F0.imprint","IMPRINT",FACE,{"disambiguationData":[TD([[makeQuery(id+"F0.imprint","IMPRINT",EDGE,{"disambiguationData":[TD([[subQ2,-1.0]])],"derivedFrom":subQ1}),1.0]])]});}
            var Q77;
            {var subQ0=sQuery(id+"F0.wireOp",EDGE,"E30.2.27");var subQ1=sQuery(id+"F0.wireOp",EDGE,"E30.2.13");var subQ2=makeQuery(id+"F0.imprint","INTERSECT",VERTEX,{"derivedFrom":[subQ1,subQ0]});Q77=makeQuery(id+"F0.imprint","IMPRINT",FACE,{"disambiguationData":[TD([[makeQuery(id+"F0.imprint","IMPRINT",EDGE,{"disambiguationData":[TD([[subQ2,-1.0]])],"derivedFrom":subQ1}),1.0]])]});}
            var Q78;
            {var subQ0=sQuery(id+"F0.wireOp",EDGE,"E27.MirrorCS");var subQ1=sQuery(id+"F0.wireOp",EDGE,"E3");var subQ2=makeQuery(id+"F0.imprint","INTERSECT",VERTEX,{"derivedFrom":[subQ1,subQ0]});Q78=makeQuery(id+"F0.imprint","IMPRINT",FACE,{"disambiguationData":[TD([[makeQuery(id+"F0.imprint","IMPRINT",EDGE,{"disambiguationData":[TD([[subQ2,-1.0]])],"derivedFrom":subQ1}),1.0]])]});}
            var Q79;
            {var subQ0=sQuery(id+"F0.wireOp",EDGE,"E30.1.27");var subQ1=sQuery(id+"F0.wireOp",EDGE,"E30.1.13");var subQ2=makeQuery(id+"F0.imprint","INTERSECT",VERTEX,{"derivedFrom":[subQ1,subQ0]});Q79=makeQuery(id+"F0.imprint","IMPRINT",FACE,{"disambiguationData":[TD([[makeQuery(id+"F0.imprint","IMPRINT",EDGE,{"disambiguationData":[TD([[subQ2,-1.0]])],"derivedFrom":subQ1}),1.0]])]});}
            var Q80;
            {var subQ0=sQuery(id+"F0.wireOp",EDGE,"E14");var subQ1=sQuery(id+"F0.wireOp",EDGE,"E3");var subQ2=makeQuery(id+"F0.imprint","INTERSECT",VERTEX,{"derivedFrom":[subQ1,subQ0]});Q80=makeQuery(id+"F0.imprint","IMPRINT",FACE,{"disambiguationData":[TD([[makeQuery(id+"F0.imprint","IMPRINT",EDGE,{"disambiguationData":[TD([[subQ2,-1.0]])],"derivedFrom":subQ1}),1.0]])]});}
            var Q81;
            {var subQ0=sQuery(id+"F0.wireOp",EDGE,"E30.2.24");var subQ1=sQuery(id+"F0.wireOp",EDGE,"E30.2.1");var subQ2=makeQuery(id+"F0.imprint","INTERSECT",VERTEX,{"derivedFrom":[subQ1,subQ0]});Q81=makeQuery(id+"F0.imprint","IMPRINT",FACE,{"disambiguationData":[TD([[makeQuery(id+"F0.imprint","IMPRINT",EDGE,{"disambiguationData":[TD([[subQ2,-1.0]])],"derivedFrom":subQ1}),-1.0]])]});}
            var Q82;
            {var subQ0=sQuery(id+"F0.wireOp",EDGE,"E30.1.24");var subQ1=sQuery(id+"F0.wireOp",EDGE,"E30.1.1");var subQ2=makeQuery(id+"F0.imprint","INTERSECT",VERTEX,{"derivedFrom":[subQ1,subQ0]});Q82=makeQuery(id+"F0.imprint","IMPRINT",FACE,{"disambiguationData":[TD([[makeQuery(id+"F0.imprint","IMPRINT",EDGE,{"disambiguationData":[TD([[subQ2,-1.0]])],"derivedFrom":subQ1}),-1.0]])]});}
            var Q83;
            {var subQ0=sQuery(id+"F0.wireOp",EDGE,"E16");var subQ1=sQuery(id+"F0.wireOp",EDGE,"E3");var subQ2=makeQuery(id+"F0.imprint","INTERSECT",VERTEX,{"derivedFrom":[subQ1,subQ0]});Q83=makeQuery(id+"F0.imprint","IMPRINT",FACE,{"disambiguationData":[TD([[makeQuery(id+"F0.imprint","IMPRINT",EDGE,{"disambiguationData":[TD([[subQ2,-1.0]])],"derivedFrom":subQ1}),-1.0]])]});}
            extrude(context, id + "F1", {"entities" : qUnion([Q0, Q1, Q2, Q3, Q4, Q5, Q6, Q7, Q8, Q9, Q10, Q11, Q12, Q13, Q14, Q15, Q16, Q17, Q18, Q19, Q20, Q21, Q22, Q23, Q24, Q25, Q26, Q27, Q28, Q29, Q30, Q31, Q32, Q33, Q34, Q35, Q36, Q37, Q38, Q39, Q40, Q41, Q42, Q43, Q44, Q45, Q46, Q47, Q48, Q49, Q50, Q51, Q52, Q53, Q54, Q55, Q56, Q57, Q58, Q59, Q60, Q61, Q62, Q63, Q64, Q65, Q66, Q67, Q68, Q69, Q70, Q71, Q72, Q73, Q74, Q75, Q76, Q77, Q78, Q79, Q80, Q81, Q82, Q83]), "depth" : 7 * mm, "offsetDistance" : 25 * mm});
        }
        {
            var Q0;
            Q0=makeQuery(id+"F1.opExtrude","SWEPT_EDGE",EDGE,{"disambiguationData":[OSD([sQuery(id+"F0.wireOp",EDGE,"E4"),sQuery(id+"F0.wireOp",EDGE,"E40.MirrorCS")])]});
            var Q1;
            Q1=makeQuery(id+"F1.opExtrude","SWEPT_EDGE",EDGE,{"disambiguationData":[OSD([sQuery(id+"F0.wireOp",EDGE,"E5"),sQuery(id+"F0.wireOp",EDGE,"E32"),sQuery(id+"F0.wireOp",EDGE,"E33.MirrorCS")])]});
            var Q2;
            Q2=makeQuery(id+"F1.opExtrude","SWEPT_EDGE",EDGE,{"disambiguationData":[OSD([sQuery(id+"F0.wireOp",EDGE,"E30.2.12"),sQuery(id+"F0.wireOp",EDGE,"E32"),sQuery(id+"F0.wireOp",EDGE,"E38.MirrorCS")])]});
            var Q3;
            Q3=makeQuery(id+"F1.opExtrude","SWEPT_EDGE",EDGE,{"disambiguationData":[OSD([sQuery(id+"F0.wireOp",EDGE,"E30.1.11"),sQuery(id+"F0.wireOp",EDGE,"E44.MirrorCS")])]});
            var Q4;
            Q4=makeQuery(id+"F1.opExtrude","SWEPT_EDGE",EDGE,{"disambiguationData":[OSD([sQuery(id+"F0.wireOp",EDGE,"E30.1.12"),sQuery(id+"F0.wireOp",EDGE,"E32"),sQuery(id+"F0.wireOp",EDGE,"E46.MirrorCS")])]});
            var Q5;
            Q5=makeQuery(id+"F1.opExtrude","SWEPT_EDGE",EDGE,{"disambiguationData":[OSD([sQuery(id+"F0.wireOp",EDGE,"E30.2.11"),sQuery(id+"F0.wireOp",EDGE,"E32"),sQuery(id+"F0.wireOp",EDGE,"E50.MirrorCS")])]});
            fillet(context, id + "F2", {"entities" : qUnion([Q0, Q1, Q2, Q3, Q4, Q5]), "radius" : .5 * mm, "tangentPropagation" : true, "allowEdgeOverflow" : false});
        }
        {
            var Q0;
            Q0=makeQuery(id+"F1.opExtrude","CAP_FACE",FACE,{"disambiguationData":[OSD([sQuery(id+"F0.wireOp",EDGE,"E0"),sQuery(id+"F0.wireOp",EDGE,"E1"),sQuery(id+"F0.wireOp",EDGE,"E2"),sQuery(id+"F0.wireOp",EDGE,"E3"),sQuery(id+"F0.wireOp",EDGE,"E4"),sQuery(id+"F0.wireOp",EDGE,"E5"),sQuery(id+"F0.wireOp",EDGE,"E6"),sQuery(id+"F0.wireOp",EDGE,"E7"),sQuery(id+"F0.wireOp",EDGE,"E8"),sQuery(id+"F0.wireOp",EDGE,"E9"),sQuery(id+"F0.wireOp",EDGE,"E10"),sQuery(id+"F0.wireOp",EDGE,"E11"),sQuery(id+"F0.wireOp",EDGE,"E14"),sQuery(id+"F0.wireOp",EDGE,"E15"),sQuery(id+"F0.wireOp",EDGE,"E16"),sQuery(id+"F0.wireOp",EDGE,"E18"),sQuery(id+"F0.wireOp",EDGE,"E19"),sQuery(id+"F0.wireOp",EDGE,"E20"),sQuery(id+"F0.wireOp",EDGE,"E21.MirrorCS"),sQuery(id+"F0.wireOp",EDGE,"E22.MirrorCS"),sQuery(id+"F0.wireOp",EDGE,"E23.MirrorCS"),sQuery(id+"F0.wireOp",EDGE,"E24.MirrorCS"),sQuery(id+"F0.wireOp",EDGE,"E25.MirrorCS"),sQuery(id+"F0.wireOp",EDGE,"E26.MirrorCS"),sQuery(id+"F0.wireOp",EDGE,"E27.MirrorCS"),sQuery(id+"F0.wireOp",EDGE,"E28.MirrorCS"),sQuery(id+"F0.wireOp",EDGE,"E29.MirrorCS"),sQuery(id+"F0.wireOp",EDGE,"E30.1.0"),sQuery(id+"F0.wireOp",EDGE,"E30.1.1"),sQuery(id+"F0.wireOp",EDGE,"E30.1.2"),sQuery(id+"F0.wireOp",EDGE,"E30.1.3"),sQuery(id+"F0.wireOp",EDGE,"E30.1.4"),sQuery(id+"F0.wireOp",EDGE,"E30.1.5"),sQuery(id+"F0.wireOp",EDGE,"E30.1.6"),sQuery(id+"F0.wireOp",EDGE,"E30.1.7"),sQuery(id+"F0.wireOp",EDGE,"E30.1.8"),sQuery(id+"F0.wireOp",EDGE,"E30.1.10"),sQuery(id+"F0.wireOp",EDGE,"E30.1.11"),sQuery(id+"F0.wireOp",EDGE,"E30.1.12"),sQuery(id+"F0.wireOp",EDGE,"E30.1.13"),sQuery(id+"F0.wireOp",EDGE,"E30.1.14"),sQuery(id+"F0.wireOp",EDGE,"E30.1.15"),sQuery(id+"F0.wireOp",EDGE,"E30.1.16"),sQuery(id+"F0.wireOp",EDGE,"E30.1.17"),sQuery(id+"F0.wireOp",EDGE,"E30.1.19"),sQuery(id+"F0.wireOp",EDGE,"E30.1.20"),sQuery(id+"F0.wireOp",EDGE,"E30.1.21"),sQuery(id+"F0.wireOp",EDGE,"E30.1.22"),sQuery(id+"F0.wireOp",EDGE,"E30.1.23"),sQuery(id+"F0.wireOp",EDGE,"E30.1.24"),sQuery(id+"F0.wireOp",EDGE,"E30.1.25"),sQuery(id+"F0.wireOp",EDGE,"E30.1.26"),sQuery(id+"F0.wireOp",EDGE,"E30.1.27"),sQuery(id+"F0.wireOp",EDGE,"E30.1.28"),sQuery(id+"F0.wireOp",EDGE,"E30.2.0"),sQuery(id+"F0.wireOp",EDGE,"E30.2.1"),sQuery(id+"F0.wireOp",EDGE,"E30.2.2"),sQuery(id+"F0.wireOp",EDGE,"E30.2.3"),sQuery(id+"F0.wireOp",EDGE,"E30.2.4"),sQuery(id+"F0.wireOp",EDGE,"E30.2.5"),sQuery(id+"F0.wireOp",EDGE,"E30.2.6"),sQuery(id+"F0.wireOp",EDGE,"E30.2.7"),sQuery(id+"F0.wireOp",EDGE,"E30.2.8"),sQuery(id+"F0.wireOp",EDGE,"E30.2.10"),sQuery(id+"F0.wireOp",EDGE,"E30.2.11"),sQuery(id+"F0.wireOp",EDGE,"E30.2.12"),sQuery(id+"F0.wireOp",EDGE,"E30.2.13"),sQuery(id+"F0.wireOp",EDGE,"E30.2.14"),sQuery(id+"F0.wireOp",EDGE,"E30.2.15"),sQuery(id+"F0.wireOp",EDGE,"E30.2.16"),sQuery(id+"F0.wireOp",EDGE,"E30.2.17"),sQuery(id+"F0.wireOp",EDGE,"E30.2.19"),sQuery(id+"F0.wireOp",EDGE,"E30.2.20"),sQuery(id+"F0.wireOp",EDGE,"E30.2.21"),sQuery(id+"F0.wireOp",EDGE,"E30.2.22"),sQuery(id+"F0.wireOp",EDGE,"E30.2.23"),sQuery(id+"F0.wireOp",EDGE,"E30.2.24"),sQuery(id+"F0.wireOp",EDGE,"E30.2.25"),sQuery(id+"F0.wireOp",EDGE,"E30.2.26"),sQuery(id+"F0.wireOp",EDGE,"E30.2.27"),sQuery(id+"F0.wireOp",EDGE,"E30.2.28"),sQuery(id+"F0.wireOp",EDGE,"E31"),sQuery(id+"F0.wireOp",EDGE,"E33.MirrorCS"),sQuery(id+"F0.wireOp",EDGE,"E34.MirrorCS"),sQuery(id+"F0.wireOp",EDGE,"E35.MirrorCS"),sQuery(id+"F0.wireOp",EDGE,"E36.MirrorCS"),sQuery(id+"F0.wireOp",EDGE,"E37.MirrorCS"),sQuery(id+"F0.wireOp",EDGE,"E38.MirrorCS"),sQuery(id+"F0.wireOp",EDGE,"E39.MirrorCS"),sQuery(id+"F0.wireOp",EDGE,"E40.MirrorCS"),sQuery(id+"F0.wireOp",EDGE,"E41.MirrorCS"),sQuery(id+"F0.wireOp",EDGE,"E42.MirrorCS"),sQuery(id+"F0.wireOp",EDGE,"E43.MirrorCS"),sQuery(id+"F0.wireOp",EDGE,"E44.MirrorCS"),sQuery(id+"F0.wireOp",EDGE,"E45.MirrorCS"),sQuery(id+"F0.wireOp",EDGE,"E46.MirrorCS"),sQuery(id+"F0.wireOp",EDGE,"E47.MirrorCS"),sQuery(id+"F0.wireOp",EDGE,"E48.MirrorCS"),sQuery(id+"F0.wireOp",EDGE,"E49.MirrorCS"),sQuery(id+"F0.wireOp",EDGE,"E50.MirrorCS")])],"isStart":false});
            var Q1;
            Q1=makeQuery(id+"F1.opExtrude","CAP_FACE",FACE,{"disambiguationData":[OSD([sQuery(id+"F0.wireOp",EDGE,"E0"),sQuery(id+"F0.wireOp",EDGE,"E1"),sQuery(id+"F0.wireOp",EDGE,"E2"),sQuery(id+"F0.wireOp",EDGE,"E3"),sQuery(id+"F0.wireOp",EDGE,"E4"),sQuery(id+"F0.wireOp",EDGE,"E5"),sQuery(id+"F0.wireOp",EDGE,"E6"),sQuery(id+"F0.wireOp",EDGE,"E7"),sQuery(id+"F0.wireOp",EDGE,"E8"),sQuery(id+"F0.wireOp",EDGE,"E9"),sQuery(id+"F0.wireOp",EDGE,"E10"),sQuery(id+"F0.wireOp",EDGE,"E11"),sQuery(id+"F0.wireOp",EDGE,"E14"),sQuery(id+"F0.wireOp",EDGE,"E15"),sQuery(id+"F0.wireOp",EDGE,"E16"),sQuery(id+"F0.wireOp",EDGE,"E18"),sQuery(id+"F0.wireOp",EDGE,"E19"),sQuery(id+"F0.wireOp",EDGE,"E20"),sQuery(id+"F0.wireOp",EDGE,"E21.MirrorCS"),sQuery(id+"F0.wireOp",EDGE,"E22.MirrorCS"),sQuery(id+"F0.wireOp",EDGE,"E23.MirrorCS"),sQuery(id+"F0.wireOp",EDGE,"E24.MirrorCS"),sQuery(id+"F0.wireOp",EDGE,"E25.MirrorCS"),sQuery(id+"F0.wireOp",EDGE,"E26.MirrorCS"),sQuery(id+"F0.wireOp",EDGE,"E27.MirrorCS"),sQuery(id+"F0.wireOp",EDGE,"E28.MirrorCS"),sQuery(id+"F0.wireOp",EDGE,"E29.MirrorCS"),sQuery(id+"F0.wireOp",EDGE,"E30.1.0"),sQuery(id+"F0.wireOp",EDGE,"E30.1.1"),sQuery(id+"F0.wireOp",EDGE,"E30.1.2"),sQuery(id+"F0.wireOp",EDGE,"E30.1.3"),sQuery(id+"F0.wireOp",EDGE,"E30.1.4"),sQuery(id+"F0.wireOp",EDGE,"E30.1.5"),sQuery(id+"F0.wireOp",EDGE,"E30.1.6"),sQuery(id+"F0.wireOp",EDGE,"E30.1.7"),sQuery(id+"F0.wireOp",EDGE,"E30.1.8"),sQuery(id+"F0.wireOp",EDGE,"E30.1.10"),sQuery(id+"F0.wireOp",EDGE,"E30.1.11"),sQuery(id+"F0.wireOp",EDGE,"E30.1.12"),sQuery(id+"F0.wireOp",EDGE,"E30.1.13"),sQuery(id+"F0.wireOp",EDGE,"E30.1.14"),sQuery(id+"F0.wireOp",EDGE,"E30.1.15"),sQuery(id+"F0.wireOp",EDGE,"E30.1.16"),sQuery(id+"F0.wireOp",EDGE,"E30.1.17"),sQuery(id+"F0.wireOp",EDGE,"E30.1.19"),sQuery(id+"F0.wireOp",EDGE,"E30.1.20"),sQuery(id+"F0.wireOp",EDGE,"E30.1.21"),sQuery(id+"F0.wireOp",EDGE,"E30.1.22"),sQuery(id+"F0.wireOp",EDGE,"E30.1.23"),sQuery(id+"F0.wireOp",EDGE,"E30.1.24"),sQuery(id+"F0.wireOp",EDGE,"E30.1.25"),sQuery(id+"F0.wireOp",EDGE,"E30.1.26"),sQuery(id+"F0.wireOp",EDGE,"E30.1.27"),sQuery(id+"F0.wireOp",EDGE,"E30.1.28"),sQuery(id+"F0.wireOp",EDGE,"E30.2.0"),sQuery(id+"F0.wireOp",EDGE,"E30.2.1"),sQuery(id+"F0.wireOp",EDGE,"E30.2.2"),sQuery(id+"F0.wireOp",EDGE,"E30.2.3"),sQuery(id+"F0.wireOp",EDGE,"E30.2.4"),sQuery(id+"F0.wireOp",EDGE,"E30.2.5"),sQuery(id+"F0.wireOp",EDGE,"E30.2.6"),sQuery(id+"F0.wireOp",EDGE,"E30.2.7"),sQuery(id+"F0.wireOp",EDGE,"E30.2.8"),sQuery(id+"F0.wireOp",EDGE,"E30.2.10"),sQuery(id+"F0.wireOp",EDGE,"E30.2.11"),sQuery(id+"F0.wireOp",EDGE,"E30.2.12"),sQuery(id+"F0.wireOp",EDGE,"E30.2.13"),sQuery(id+"F0.wireOp",EDGE,"E30.2.14"),sQuery(id+"F0.wireOp",EDGE,"E30.2.15"),sQuery(id+"F0.wireOp",EDGE,"E30.2.16"),sQuery(id+"F0.wireOp",EDGE,"E30.2.17"),sQuery(id+"F0.wireOp",EDGE,"E30.2.19"),sQuery(id+"F0.wireOp",EDGE,"E30.2.20"),sQuery(id+"F0.wireOp",EDGE,"E30.2.21"),sQuery(id+"F0.wireOp",EDGE,"E30.2.22"),sQuery(id+"F0.wireOp",EDGE,"E30.2.23"),sQuery(id+"F0.wireOp",EDGE,"E30.2.24"),sQuery(id+"F0.wireOp",EDGE,"E30.2.25"),sQuery(id+"F0.wireOp",EDGE,"E30.2.26"),sQuery(id+"F0.wireOp",EDGE,"E30.2.27"),sQuery(id+"F0.wireOp",EDGE,"E30.2.28"),sQuery(id+"F0.wireOp",EDGE,"E31"),sQuery(id+"F0.wireOp",EDGE,"E33.MirrorCS"),sQuery(id+"F0.wireOp",EDGE,"E34.MirrorCS"),sQuery(id+"F0.wireOp",EDGE,"E35.MirrorCS"),sQuery(id+"F0.wireOp",EDGE,"E36.MirrorCS"),sQuery(id+"F0.wireOp",EDGE,"E37.MirrorCS"),sQuery(id+"F0.wireOp",EDGE,"E38.MirrorCS"),sQuery(id+"F0.wireOp",EDGE,"E39.MirrorCS"),sQuery(id+"F0.wireOp",EDGE,"E40.MirrorCS"),sQuery(id+"F0.wireOp",EDGE,"E41.MirrorCS"),sQuery(id+"F0.wireOp",EDGE,"E42.MirrorCS"),sQuery(id+"F0.wireOp",EDGE,"E43.MirrorCS"),sQuery(id+"F0.wireOp",EDGE,"E44.MirrorCS"),sQuery(id+"F0.wireOp",EDGE,"E45.MirrorCS"),sQuery(id+"F0.wireOp",EDGE,"E46.MirrorCS"),sQuery(id+"F0.wireOp",EDGE,"E47.MirrorCS"),sQuery(id+"F0.wireOp",EDGE,"E48.MirrorCS"),sQuery(id+"F0.wireOp",EDGE,"E49.MirrorCS"),sQuery(id+"F0.wireOp",EDGE,"E50.MirrorCS")])],"isStart":true});
            fillet(context, id + "F3", {"entities" : qUnion([Q0, Q1]), "radius" : .5 * mm, "tangentPropagation" : true, "allowEdgeOverflow" : false});
        }
        {
            var Q0;
            Q0=makeQuery(id+"F1.opExtrude","SWEPT_FACE",FACE,{"disambiguationData":[OSD([sQuery(id+"F0.wireOp",EDGE,"E30.1.0")])]});
            var Q1;
            Q1=makeQuery(id+"F1.opExtrude","SWEPT_FACE",FACE,{"disambiguationData":[OSD([sQuery(id+"F0.wireOp",EDGE,"E30.1.2")])]});
            var Q2;
            Q2=makeQuery(id+"F1.opExtrude","SWEPT_FACE",FACE,{"disambiguationData":[OSD([sQuery(id+"F0.wireOp",EDGE,"E30.1.22")])]});
            var Q3;
            Q3=makeQuery(id+"F1.opExtrude","SWEPT_FACE",FACE,{"disambiguationData":[OSD([sQuery(id+"F0.wireOp",EDGE,"E30.1.7")])]});
            var Q4;
            Q4=makeQuery(id+"F1.opExtrude","SWEPT_FACE",FACE,{"disambiguationData":[OSD([sQuery(id+"F0.wireOp",EDGE,"E30.1.17")])]});
            var Q5;
            {var subQ0=sQuery(id+"F0.wireOp",EDGE,"E30.1.3");Q5=makeQuery(id+"F3.opFillet","BLEND_EDGE",EDGE,{"blendedFrom":[makeQuery(id+"F1.opExtrude","CAP_EDGE",EDGE,{"disambiguationData":[OSD([subQ0])],"isStart":true}),makeQuery(id+"F1.opExtrude","SWEPT_FACE",FACE,{"disambiguationData":[OSD([subQ0])]})],"blendedInto":[makeQuery(id+"F1.opExtrude","SWEPT_FACE",FACE,{"disambiguationData":[OSD([subQ0])]})]});}
            var Q6;
            Q6=makeQuery(id+"F1.opExtrude","SWEPT_FACE",FACE,{"disambiguationData":[OSD([sQuery(id+"F0.wireOp",EDGE,"E30.1.3")])]});
            var Q7;
            Q7=makeQuery(id+"F1.opExtrude","SWEPT_FACE",FACE,{"disambiguationData":[OSD([sQuery(id+"F0.wireOp",EDGE,"E30.1.4")])]});
            var Q8;
            Q8=makeQuery(id+"F1.opExtrude","SWEPT_FACE",FACE,{"disambiguationData":[OSD([sQuery(id+"F0.wireOp",EDGE,"E30.2.4")])]});
            var Q9;
            Q9=makeQuery(id+"F1.opExtrude","SWEPT_FACE",FACE,{"disambiguationData":[OSD([sQuery(id+"F0.wireOp",EDGE,"E30.2.3")])]});
            var Q10;
            Q10=makeQuery(id+"F1.opExtrude","SWEPT_FACE",FACE,{"disambiguationData":[OSD([sQuery(id+"F0.wireOp",EDGE,"E30.2.17")])]});
            var Q11;
            Q11=makeQuery(id+"F1.opExtrude","SWEPT_FACE",FACE,{"disambiguationData":[OSD([sQuery(id+"F0.wireOp",EDGE,"E30.2.7")])]});
            var Q12;
            Q12=makeQuery(id+"F1.opExtrude","SWEPT_FACE",FACE,{"disambiguationData":[OSD([sQuery(id+"F0.wireOp",EDGE,"E30.2.0")])]});
            var Q13;
            Q13=makeQuery(id+"F1.opExtrude","SWEPT_FACE",FACE,{"disambiguationData":[OSD([sQuery(id+"F0.wireOp",EDGE,"E30.2.2")])]});
            var Q14;
            Q14=makeQuery(id+"F1.opExtrude","SWEPT_FACE",FACE,{"disambiguationData":[OSD([sQuery(id+"F0.wireOp",EDGE,"E30.2.22")])]});
            var Q15;
            Q15=makeQuery(id+"F1.opExtrude","SWEPT_FACE",FACE,{"disambiguationData":[OSD([sQuery(id+"F0.wireOp",EDGE,"E28.MirrorCS")])]});
            var Q16;
            Q16=makeQuery(id+"F1.opExtrude","SWEPT_FACE",FACE,{"disambiguationData":[OSD([sQuery(id+"F0.wireOp",EDGE,"E25.MirrorCS")])]});
            var Q17;
            Q17=makeQuery(id+"F1.opExtrude","SWEPT_FACE",FACE,{"disambiguationData":[OSD([sQuery(id+"F0.wireOp",EDGE,"E21.MirrorCS")])]});
            var Q18;
            Q18=makeQuery(id+"F1.opExtrude","SWEPT_FACE",FACE,{"disambiguationData":[OSD([sQuery(id+"F0.wireOp",EDGE,"E7")])]});
            var Q19;
            Q19=makeQuery(id+"F1.opExtrude","SWEPT_FACE",FACE,{"disambiguationData":[OSD([sQuery(id+"F0.wireOp",EDGE,"E10")])]});
            var Q20;
            Q20=makeQuery(id+"F1.opExtrude","SWEPT_FACE",FACE,{"disambiguationData":[OSD([sQuery(id+"F0.wireOp",EDGE,"E15")])]});
            var Q21;
            Q21=makeQuery(id+"F1.opExtrude","SWEPT_FACE",FACE,{"disambiguationData":[OSD([sQuery(id+"F0.wireOp",EDGE,"E19")])]});
            var Q22;
            Q22=makeQuery(id+"F1.opExtrude","SWEPT_FACE",FACE,{"disambiguationData":[OSD([sQuery(id+"F0.wireOp",EDGE,"E39.MirrorCS")])]});
            var Q23;
            Q23=makeQuery(id+"F1.opExtrude","SWEPT_FACE",FACE,{"disambiguationData":[OSD([sQuery(id+"F0.wireOp",EDGE,"E43.MirrorCS")])]});
            var Q24;
            Q24=makeQuery(id+"F1.opExtrude","SWEPT_FACE",FACE,{"disambiguationData":[OSD([sQuery(id+"F0.wireOp",EDGE,"E34.MirrorCS")])]});
            var Q25;
            Q25=makeQuery(id+"F1.opExtrude","SWEPT_FACE",FACE,{"disambiguationData":[OSD([sQuery(id+"F0.wireOp",EDGE,"E37.MirrorCS")])]});
            var Q26;
            Q26=makeQuery(id+"F1.opExtrude","SWEPT_FACE",FACE,{"disambiguationData":[OSD([sQuery(id+"F0.wireOp",EDGE,"E49.MirrorCS")])]});
            var Q27;
            Q27=makeQuery(id+"F1.opExtrude","SWEPT_FACE",FACE,{"disambiguationData":[OSD([sQuery(id+"F0.wireOp",EDGE,"E45.MirrorCS")])]});
            fillet(context, id + "F4", {"entities" : qUnion([Q0, Q1, Q2, Q3, Q4, Q5, Q6, Q7, Q8, Q9, Q10, Q11, Q12, Q13, Q14, Q15, Q16, Q17, Q18, Q19, Q20, Q21, Q22, Q23, Q24, Q25, Q26, Q27]), "radius" : .5 * mm, "tangentPropagation" : true, "allowEdgeOverflow" : false});
        }
    });
